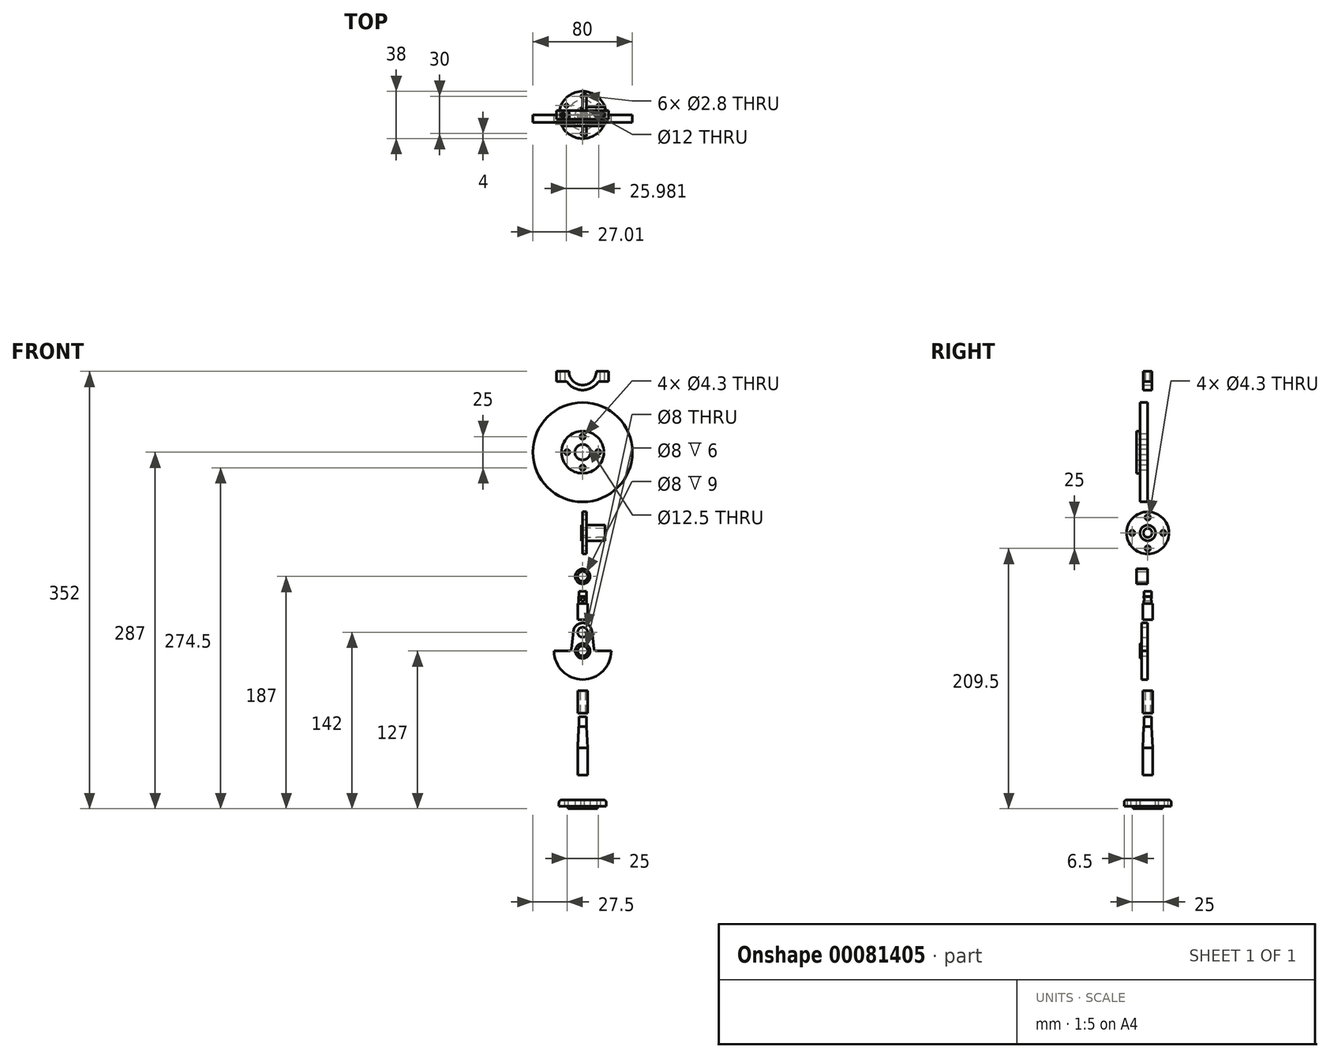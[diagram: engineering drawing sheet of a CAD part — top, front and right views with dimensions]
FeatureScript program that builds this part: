
annotation { "Feature Type Name" : "Feature", "Feature Type Description" : "" }
export const myFeature = defineFeature(function(context is Context, id is Id, definition is map)
    precondition{}
    {
        {
            var Q0;
            Q0=qCreatedBy(makeId("Top.planeOp"),FACE);
            var sketch = newSketch(context, id + "F0", { "sketchPlane" : qUnion([Q0])});
            skCircle(sketch, "E0", {"center": v(0, 0) * mm, "radius": 19 * mm});
            skCircle(sketch, "E1", {"center": v(0, 0) * mm, "radius": 6 * mm});
            skSolve(sketch);
        }
        {
            var Q0;
            Q0 = qSketchRegion(id + "F0", true);
            extrude(context, id + "F1", {"entities" : qUnion([Q0]), "depth" : 5 * mm});
        }
        {
            var Q0;
            Q0=makeQuery(id+"F1.opExtrude","CAP_FACE",FACE,{"disambiguationData":[OSD([sQuery(id+"F0.wireOp",EDGE,"E0"),sQuery(id+"F0.wireOp",EDGE,"E1")])],"isStart":true});
            var sketch = newSketch(context, id + "F2", { "sketchPlane" : qUnion([Q0])});
            skCircle(sketch, "E2", {"center": v(0, 0) * mm, "radius": 6 * mm});
            skCircle(sketch, "E3", {"center": v(0, 0) * mm, "radius": 12 * mm});
            skSolve(sketch);
        }
        {
            var Q0;
            Q0 = qSketchRegion(id + "F2", true);
            extrude(context, id + "F3", {"entities" : qUnion([Q0]), "operationType" : NewBodyOperationType.ADD, "depth" : 2 * mm});
        }
        {
            var Q0;
            Q0=makeQuery(id+"F1.opExtrude","CAP_EDGE",EDGE,{"disambiguationData":[OSD([sQuery(id+"F0.wireOp",EDGE,"E0")])],"isStart":false});
            fillet(context, id + "F4", {"entities" : qUnion([Q0]), "radius" : 2 * mm, "tangentPropagation" : true, "allowEdgeOverflow" : false});
        }
        {
            var Q0;
            Q0=makeQuery(id+"F1.opExtrude","CAP_FACE",FACE,{"disambiguationData":[OSD([sQuery(id+"F0.wireOp",EDGE,"E0"),sQuery(id+"F0.wireOp",EDGE,"E1")])],"isStart":false});
            var sketch = newSketch(context, id + "F5", { "sketchPlane" : qUnion([Q0])});
            skLineSegment(sketch, "E4", {"start": v(0, 0) * mm, "end": v(0, 15) * mm});
            skLineSegment(sketch, "E5.0", {"start": v(0, 15) * mm, "end": v(13, 7.5) * mm});
            skLineSegment(sketch, "E5.1", {"start": v(13, 7.5) * mm, "end": v(13, -7.5) * mm});
            skLineSegment(sketch, "E5.2", {"start": v(13, -7.5) * mm, "end": v(0, -15) * mm});
            skLineSegment(sketch, "E5.3", {"start": v(0, -15) * mm, "end": v(-13, -7.5) * mm});
            skLineSegment(sketch, "E5.4", {"start": v(-13, -7.5) * mm, "end": v(-13, 7.5) * mm});
            skLineSegment(sketch, "E5.5", {"start": v(-13, 7.5) * mm, "end": v(0, 15) * mm});
            skCircle(sketch, "E6", {"center": v(0, 15) * mm, "radius": 1.4 * mm});
            skCircle(sketch, "E7", {"center": v(-13, 7.5) * mm, "radius": 1.4 * mm});
            skCircle(sketch, "E8", {"center": v(-13, -7.5) * mm, "radius": 1.4 * mm});
            skCircle(sketch, "E9", {"center": v(0, -15) * mm, "radius": 1.4 * mm});
            skCircle(sketch, "E10", {"center": v(13, -7.5) * mm, "radius": 1.4 * mm});
            skCircle(sketch, "E11", {"center": v(13, 7.5) * mm, "radius": 1.4 * mm});
            skSolve(sketch);
        }
        {
            var Q0;
            {var subQ0=sQuery(id+"F5.wireOp",EDGE,"E5.5");var subQ1=sQuery(id+"F5.wireOp",EDGE,"E5.4");var subQ2=makeQuery(id+"F5.imprint","INTERSECT",VERTEX,{"derivedFrom":[subQ1,subQ0]});Q0=makeQuery(id+"F5.imprint","IMPRINT",FACE,{"disambiguationData":[TD([[makeQuery(id+"F5.imprint","IMPRINT",EDGE,{"disambiguationData":[TD([[subQ2,1.0]])],"derivedFrom":subQ1}),1.0]])]});}
            var Q1;
            {var subQ0=sQuery(id+"F5.wireOp",EDGE,"E5.5");var subQ1=sQuery(id+"F5.wireOp",EDGE,"E5.4");var subQ2=makeQuery(id+"F5.imprint","INTERSECT",VERTEX,{"derivedFrom":[subQ1,subQ0]});Q1=makeQuery(id+"F5.imprint","IMPRINT",FACE,{"disambiguationData":[TD([[makeQuery(id+"F5.imprint","IMPRINT",EDGE,{"disambiguationData":[TD([[subQ2,1.0]])],"derivedFrom":subQ1}),-1.0]])]});}
            var Q2;
            {var subQ1=sQuery(id+"F5.wireOp",EDGE,"E5.0");var subQ3=sQuery(id+"F5.wireOp",EDGE,"E6");var subQ4=makeQuery(id+"F5.imprint","INTERSECT",VERTEX,{"derivedFrom":[subQ1,subQ3]});Q2=makeQuery(id+"F5.imprint","IMPRINT",FACE,{"disambiguationData":[TD([[makeQuery(id+"F5.imprint","IMPRINT",EDGE,{"disambiguationData":[TD([[subQ4,-1.0]])],"derivedFrom":subQ3}),1.0]])]});}
            var Q3;
            {var subQ1=sQuery(id+"F5.wireOp",EDGE,"E4");var subQ3=sQuery(id+"F5.wireOp",EDGE,"E6");var subQ4=makeQuery(id+"F5.imprint","INTERSECT",VERTEX,{"derivedFrom":[subQ1,subQ3]});Q3=makeQuery(id+"F5.imprint","IMPRINT",FACE,{"disambiguationData":[TD([[makeQuery(id+"F5.imprint","IMPRINT",EDGE,{"disambiguationData":[TD([[subQ4,-1.0]])],"derivedFrom":subQ3}),1.0]])]});}
            var Q4;
            {var subQ1=sQuery(id+"F5.wireOp",EDGE,"E4");var subQ3=sQuery(id+"F5.wireOp",EDGE,"E6");var subQ4=makeQuery(id+"F5.imprint","INTERSECT",VERTEX,{"derivedFrom":[subQ1,subQ3]});Q4=makeQuery(id+"F5.imprint","IMPRINT",FACE,{"disambiguationData":[TD([[makeQuery(id+"F5.imprint","IMPRINT",EDGE,{"disambiguationData":[TD([[subQ4,1.0]])],"derivedFrom":subQ3}),1.0]])]});}
            var Q5;
            {var subQ0=sQuery(id+"F5.wireOp",EDGE,"E5.1");var subQ1=sQuery(id+"F5.wireOp",EDGE,"E5.0");var subQ2=makeQuery(id+"F5.imprint","INTERSECT",VERTEX,{"derivedFrom":[subQ1,subQ0]});Q5=makeQuery(id+"F5.imprint","IMPRINT",FACE,{"disambiguationData":[TD([[makeQuery(id+"F5.imprint","IMPRINT",EDGE,{"disambiguationData":[TD([[subQ2,1.0]])],"derivedFrom":subQ1}),1.0]])]});}
            var Q6;
            {var subQ0=sQuery(id+"F5.wireOp",EDGE,"E5.1");var subQ1=sQuery(id+"F5.wireOp",EDGE,"E5.0");var subQ2=makeQuery(id+"F5.imprint","INTERSECT",VERTEX,{"derivedFrom":[subQ1,subQ0]});Q6=makeQuery(id+"F5.imprint","IMPRINT",FACE,{"disambiguationData":[TD([[makeQuery(id+"F5.imprint","IMPRINT",EDGE,{"disambiguationData":[TD([[subQ2,1.0]])],"derivedFrom":subQ1}),-1.0]])]});}
            var Q7;
            {var subQ0=sQuery(id+"F5.wireOp",EDGE,"E5.2");var subQ1=sQuery(id+"F5.wireOp",EDGE,"E5.1");var subQ2=makeQuery(id+"F5.imprint","INTERSECT",VERTEX,{"derivedFrom":[subQ1,subQ0]});Q7=makeQuery(id+"F5.imprint","IMPRINT",FACE,{"disambiguationData":[TD([[makeQuery(id+"F5.imprint","IMPRINT",EDGE,{"disambiguationData":[TD([[subQ2,1.0]])],"derivedFrom":subQ1}),1.0]])]});}
            var Q8;
            {var subQ0=sQuery(id+"F5.wireOp",EDGE,"E5.2");var subQ1=sQuery(id+"F5.wireOp",EDGE,"E5.1");var subQ2=makeQuery(id+"F5.imprint","INTERSECT",VERTEX,{"derivedFrom":[subQ1,subQ0]});Q8=makeQuery(id+"F5.imprint","IMPRINT",FACE,{"disambiguationData":[TD([[makeQuery(id+"F5.imprint","IMPRINT",EDGE,{"disambiguationData":[TD([[subQ2,1.0]])],"derivedFrom":subQ1}),-1.0]])]});}
            var Q9;
            {var subQ0=sQuery(id+"F5.wireOp",EDGE,"E5.3");var subQ1=sQuery(id+"F5.wireOp",EDGE,"E5.2");var subQ2=makeQuery(id+"F5.imprint","INTERSECT",VERTEX,{"derivedFrom":[subQ1,subQ0]});Q9=makeQuery(id+"F5.imprint","IMPRINT",FACE,{"disambiguationData":[TD([[makeQuery(id+"F5.imprint","IMPRINT",EDGE,{"disambiguationData":[TD([[subQ2,1.0]])],"derivedFrom":subQ1}),1.0]])]});}
            var Q10;
            {var subQ0=sQuery(id+"F5.wireOp",EDGE,"E5.3");var subQ1=sQuery(id+"F5.wireOp",EDGE,"E5.2");var subQ2=makeQuery(id+"F5.imprint","INTERSECT",VERTEX,{"derivedFrom":[subQ1,subQ0]});Q10=makeQuery(id+"F5.imprint","IMPRINT",FACE,{"disambiguationData":[TD([[makeQuery(id+"F5.imprint","IMPRINT",EDGE,{"disambiguationData":[TD([[subQ2,1.0]])],"derivedFrom":subQ1}),-1.0]])]});}
            var Q11;
            {var subQ0=sQuery(id+"F5.wireOp",EDGE,"E5.4");var subQ1=sQuery(id+"F5.wireOp",EDGE,"E5.3");var subQ2=makeQuery(id+"F5.imprint","INTERSECT",VERTEX,{"derivedFrom":[subQ1,subQ0]});Q11=makeQuery(id+"F5.imprint","IMPRINT",FACE,{"disambiguationData":[TD([[makeQuery(id+"F5.imprint","IMPRINT",EDGE,{"disambiguationData":[TD([[subQ2,1.0]])],"derivedFrom":subQ1}),1.0]])]});}
            var Q12;
            {var subQ0=sQuery(id+"F5.wireOp",EDGE,"E5.4");var subQ1=sQuery(id+"F5.wireOp",EDGE,"E5.3");var subQ2=makeQuery(id+"F5.imprint","INTERSECT",VERTEX,{"derivedFrom":[subQ1,subQ0]});Q12=makeQuery(id+"F5.imprint","IMPRINT",FACE,{"disambiguationData":[TD([[makeQuery(id+"F5.imprint","IMPRINT",EDGE,{"disambiguationData":[TD([[subQ2,1.0]])],"derivedFrom":subQ1}),-1.0]])]});}
            extrude(context, id + "F6", {"entities" : qUnion([Q0, Q1, Q2, Q3, Q4, Q5, Q6, Q7, Q8, Q9, Q10, Q11, Q12]), "operationType" : NewBodyOperationType.REMOVE, "oppositeDirection" : true, "depth" : 25 * mm});
        }
        {
            var Q0;
            Q0=makeQuery(id+"F1.opExtrude","SWEPT_BODY",BODY,{"disambiguationData":[OSD([sQuery(id+"F0.wireOp",EDGE,"E0"),sQuery(id+"F0.wireOp",EDGE,"E1")])]});
            transform(context, id + "F7", {"entities" : qUnion([Q0]), "transformType" : TransformType.TRANSLATION_3D, "dx" : 0 * mm, "dy" : 0 * mm, "dz" : 100 * mm, "makeCopy" : false});
        }
        {
            var Q0;
            Q0=qCreatedBy(makeId("Front.planeOp"),FACE);
            var sketch = newSketch(context, id + "F8", { "sketchPlane" : qUnion([Q0])});
            skLineSegment(sketch, "E12", {"start": v(0, 0) * mm, "end": v(0, 22) * mm});
            skLineSegment(sketch, "E13", {"start": v(0, 22) * mm, "end": v(4, 22) * mm});
            skLineSegment(sketch, "E14", {"start": v(4, 22) * mm, "end": v(4, 0) * mm});
            skLineSegment(sketch, "E15", {"start": v(4, 0) * mm, "end": v(0, 0) * mm});
            skLineSegment(sketch, "E16", {"start": v(0, 0) * mm, "end": v(0, 39) * mm});
            skLineSegment(sketch, "E17", {"start": v(0, 39) * mm, "end": v(3.18, 39) * mm});
            skLineSegment(sketch, "E18", {"start": v(3.18, 39) * mm, "end": v(4, 22) * mm});
            skLineSegment(sketch, "E19", {"start": v(0, 0) * mm, "end": v(0, 47) * mm});
            skLineSegment(sketch, "E20", {"start": v(0, 47) * mm, "end": v(3, 47) * mm});
            skLineSegment(sketch, "E21", {"start": v(3, 47) * mm, "end": v(3, 39) * mm});
            skSolve(sketch);
        }
        {
            var Q0;
            Q0 = qSketchRegion(id + "F8", true);
            var Q1;
            Q1=sQuery(id+"F8.wireOp",EDGE,"E19");
            revolve(context, id + "F9", {"entities" : qUnion([Q0]), "axis" : qUnion([Q1]), "revolveType" : RevolveType.FULL});
        }
        {
            var Q0;
            Q0=makeQuery(id+"F9.opRevolve","SWEPT_BODY",BODY,{"disambiguationData":[OSD([sQuery(id+"F8.wireOp",EDGE,"E14"),sQuery(id+"F8.wireOp",EDGE,"E15"),sQuery(id+"F8.wireOp",EDGE,"E17"),sQuery(id+"F8.wireOp",EDGE,"E18"),sQuery(id+"F8.wireOp",EDGE,"E19"),sQuery(id+"F8.wireOp",EDGE,"E20"),sQuery(id+"F8.wireOp",EDGE,"E21")])]});
            transform(context, id + "F10", {"entities" : qUnion([Q0]), "transformType" : TransformType.TRANSLATION_3D, "dx" : 0 * mm, "dy" : 0 * mm, "dz" : 125 * mm, "makeCopy" : false});
        }
        {
            var Q0;
            Q0=qCreatedBy(makeId("Top.planeOp"),FACE);
            var sketch = newSketch(context, id + "F11", { "sketchPlane" : qUnion([Q0])});
            skCircle(sketch, "E22", {"center": v(0, 0) * mm, "radius": 2 * mm});
            skCircle(sketch, "E23", {"center": v(0, 0) * mm, "radius": 4 * mm});
            skSolve(sketch);
        }
        {
            var Q0;
            Q0 = qSketchRegion(id + "F11", true);
            extrude(context, id + "F12", {"entities" : qUnion([Q0]), "depth" : 18 * mm});
        }
        {
            var Q0;
            Q0=makeQuery(id+"F12.opExtrude","SWEPT_BODY",BODY,{"disambiguationData":[OSD([sQuery(id+"F11.wireOp",EDGE,"E22"),sQuery(id+"F11.wireOp",EDGE,"E23")])]});
            transform(context, id + "F13", {"entities" : qUnion([Q0]), "transformType" : TransformType.TRANSLATION_3D, "dx" : 0 * mm, "dy" : 0 * mm, "dz" : 175 * mm, "makeCopy" : false});
        }
        {
            var Q0;
            Q0=qCreatedBy(makeId("Front.planeOp"),FACE);
            var sketch = newSketch(context, id + "F14", { "sketchPlane" : qUnion([Q0])});
            skArc(sketch, "E24", {"start": v(-23, 0) * mm, "mid": v(0, -23) * mm, "end": v(23, 0) * mm});
            skLineSegment(sketch, "E25", {"start": v(-9.3, 0) * mm, "end": v(-23, 0) * mm});
            skLineSegment(sketch, "E26", {"start": v(-23, 0) * mm, "end": v(-9.3, 0) * mm});
            skCircle(sketch, "E27", {"center": v(0, 0) * mm, "radius": 4 * mm});
            skLineSegment(sketch, "E28.trimOffspring", {"start": v(11.08, 0) * mm, "end": v(23, 0) * mm});
            skCircle(sketch, "E29", {"center": v(0, 15) * mm, "radius": 4 * mm});
            skArc(sketch, "E30", {"start": v(7.45, 15.87) * mm, "mid": v(0, 22.5) * mm, "end": v(-7.45, 15.87) * mm});
            skLineSegment(sketch, "E31", {"start": v(-23, 0) * mm, "end": v(-11.3, 0) * mm});
            skLineSegment(sketch, "E32", {"start": v(-11.3, 0) * mm, "end": v(-11.3, 2.99) * mm});
            skLineSegment(sketch, "E33", {"start": v(-11.3, 0) * mm, "end": v(-11.08, 0) * mm});
            skLineSegment(sketch, "E34", {"start": v(-9.1, 1.77) * mm, "end": v(-7.45, 15.87) * mm});
            skPoint(sketch, "E35.visualSharp", {"position": v(-9.3, 0) * mm});
            skArc(sketch, "E35.filletArc", {"start": v(-11.08, 0) * mm, "mid": v(-9.75, 0.5) * mm, "end": v(-9.1, 1.77) * mm});
            skArc(sketch, "E36.MirrorCS", {"start": v(11.08, 0) * mm, "mid": v(9.75, 0.5) * mm, "end": v(9.1, 1.77) * mm});
            skLineSegment(sketch, "E37.MirrorCS", {"start": v(9.1, 1.77) * mm, "end": v(7.45, 15.87) * mm});
            skSolve(sketch);
        }
        {
            var Q0;
            Q0=makeQuery(id+"F14.imprint","IMPRINT",FACE,{"disambiguationData":[TD([[makeQuery(id+"F14.imprint","IMPRINT",EDGE,{"derivedFrom":sQuery(id+"F14.wireOp",EDGE,"E24")}),1.0]])]});
            extrude(context, id + "F15", {"entities" : qUnion([Q0]), "depth" : 5 * mm});
        }
        {
            var Q0;
            Q0=makeQuery(id+"F15.opExtrude","CAP_FACE",FACE,{"disambiguationData":[OSD([sQuery(id+"F14.wireOp",EDGE,"E24"),sQuery(id+"F14.wireOp",EDGE,"E27"),sQuery(id+"F14.wireOp",EDGE,"E28.trimOffspring"),sQuery(id+"F14.wireOp",EDGE,"E29"),sQuery(id+"F14.wireOp",EDGE,"E30"),sQuery(id+"F14.wireOp",EDGE,"E31"),sQuery(id+"F14.wireOp",EDGE,"E33"),sQuery(id+"F14.wireOp",EDGE,"E34"),sQuery(id+"F14.wireOp",EDGE,"E35.filletArc"),sQuery(id+"F14.wireOp",EDGE,"E36.MirrorCS"),sQuery(id+"F14.wireOp",EDGE,"E37.MirrorCS")])],"isStart":false});
            var sketch = newSketch(context, id + "F16", { "sketchPlane" : qUnion([Q0])});
            skCircle(sketch, "E38", {"center": v(0, 0) * mm, "radius": 6 * mm});
            skCircle(sketch, "E39", {"center": v(0, 0) * mm, "radius": 4 * mm});
            skSolve(sketch);
        }
        {
            var Q0;
            Q0 = qSketchRegion(id + "F16", true);
            extrude(context, id + "F17", {"entities" : qUnion([Q0]), "operationType" : NewBodyOperationType.ADD, "depth" : 1 * mm});
        }
        {
            var Q0;
            Q0=makeQuery(id+"F15.opExtrude","SWEPT_BODY",BODY,{"disambiguationData":[OSD([sQuery(id+"F14.wireOp",EDGE,"E24"),sQuery(id+"F14.wireOp",EDGE,"E27"),sQuery(id+"F14.wireOp",EDGE,"E28.trimOffspring"),sQuery(id+"F14.wireOp",EDGE,"E29"),sQuery(id+"F14.wireOp",EDGE,"E30"),sQuery(id+"F14.wireOp",EDGE,"E31"),sQuery(id+"F14.wireOp",EDGE,"E33"),sQuery(id+"F14.wireOp",EDGE,"E34"),sQuery(id+"F14.wireOp",EDGE,"E35.filletArc"),sQuery(id+"F14.wireOp",EDGE,"E36.MirrorCS"),sQuery(id+"F14.wireOp",EDGE,"E37.MirrorCS")])]});
            transform(context, id + "F18", {"entities" : qUnion([Q0]), "transformType" : TransformType.TRANSLATION_3D, "dx" : 0 * mm, "dy" : 0 * mm, "dz" : 225 * mm, "makeCopy" : false});
        }
        {
            var Q0;
            Q0=qCreatedBy(makeId("Front.planeOp"),FACE);
            var sketch = newSketch(context, id + "F19", { "sketchPlane" : qUnion([Q0])});
            skLineSegment(sketch, "E40", {"start": v(0, 0) * mm, "end": v(4, 0) * mm});
            skLineSegment(sketch, "E41", {"start": v(4, 0) * mm, "end": v(4, 13) * mm});
            skLineSegment(sketch, "E42", {"start": v(4, 13) * mm, "end": v(3.17, 13) * mm});
            skLineSegment(sketch, "E43", {"start": v(0, 13) * mm, "end": v(0, 0) * mm});
            skLineSegment(sketch, "E44", {"start": v(0, 0) * mm, "end": v(0, 19) * mm});
            skLineSegment(sketch, "E45", {"start": v(3, 19) * mm, "end": v(3.17, 19) * mm});
            skLineSegment(sketch, "E46", {"start": v(3.17, 19) * mm, "end": v(3.17, 13) * mm});
            skLineSegment(sketch, "E47", {"start": v(0, 0) * mm, "end": v(0, 23) * mm});
            skLineSegment(sketch, "E48", {"start": v(0, 23) * mm, "end": v(3, 23) * mm});
            skLineSegment(sketch, "E49", {"start": v(3, 23) * mm, "end": v(3, 19) * mm});
            skSolve(sketch);
        }
        {
            var Q0;
            Q0 = qSketchRegion(id + "F19", true);
            var Q1;
            Q1=sQuery(id+"F19.wireOp",EDGE,"E47");
            revolve(context, id + "F20", {"entities" : qUnion([Q0]), "axis" : qUnion([Q1]), "revolveType" : RevolveType.FULL});
        }
        {
            var Q0;
            Q0=qCreatedBy(makeId("Front.planeOp"),FACE);
            var sketch = newSketch(context, id + "F21", { "sketchPlane" : qUnion([Q0])});
            skLineSegment(sketch, "E50", {"start": v(0, 0) * mm, "end": v(0, 16.55) * mm});
            skCircle(sketch, "E51", {"center": v(0, 16.55) * mm, "radius": 1.5 * mm});
            skSolve(sketch);
        }
        {
            var Q0;
            Q0 = qSketchRegion(id + "F21", true);
            extrude(context, id + "F22", {"entities" : qUnion([Q0]), "operationType" : NewBodyOperationType.REMOVE, "endBound" : BoundingType.SYMMETRIC, "oppositeDirection" : true, "depth" : 25 * mm});
        }
        {
            var Q0;
            Q0=makeQuery(id+"F20.opRevolve","SWEPT_BODY",BODY,{"disambiguationData":[OSD([sQuery(id+"F19.wireOp",EDGE,"E40"),sQuery(id+"F19.wireOp",EDGE,"E41"),sQuery(id+"F19.wireOp",EDGE,"E42"),sQuery(id+"F19.wireOp",EDGE,"E45"),sQuery(id+"F19.wireOp",EDGE,"E46"),sQuery(id+"F19.wireOp",EDGE,"E47"),sQuery(id+"F19.wireOp",EDGE,"E48"),sQuery(id+"F19.wireOp",EDGE,"E49")])]});
            transform(context, id + "F23", {"entities" : qUnion([Q0]), "transformType" : TransformType.TRANSLATION_3D, "dx" : 0 * mm, "dy" : 0 * mm, "dz" : 250 * mm, "makeCopy" : false});
        }
        {
            var Q0;
            Q0=qCreatedBy(makeId("Front.planeOp"),FACE);
            var sketch = newSketch(context, id + "F24", { "sketchPlane" : qUnion([Q0])});
            skCircle(sketch, "E52", {"center": v(0, 0) * mm, "radius": 4 * mm});
            skCircle(sketch, "E53", {"center": v(0, 0) * mm, "radius": 6 * mm});
            skSolve(sketch);
        }
        {
            var Q0;
            Q0 = qSketchRegion(id + "F24", true);
            extrude(context, id + "F25", {"entities" : qUnion([Q0]), "depth" : 9 * mm});
        }
        {
            var Q0;
            Q0=makeQuery(id+"F25.opExtrude","SWEPT_BODY",BODY,{"disambiguationData":[OSD([sQuery(id+"F24.wireOp",EDGE,"E52"),sQuery(id+"F24.wireOp",EDGE,"E53")])]});
            transform(context, id + "F26", {"entities" : qUnion([Q0]), "transformType" : TransformType.TRANSLATION_3D, "dx" : 0 * mm, "dy" : 0 * mm, "dz" : 285 * mm, "makeCopy" : false});
        }
        {
            var Q0;
            Q0=qCreatedBy(makeId("Front.planeOp"),FACE);
            var sketch = newSketch(context, id + "F27", { "sketchPlane" : qUnion([Q0])});
            skLineSegment(sketch, "E54", {"start": v(0, 0) * mm, "end": v(-1, 0) * mm});
            skLineSegment(sketch, "E55", {"start": v(-1, 0) * mm, "end": v(-1, 6.25) * mm});
            skLineSegment(sketch, "E56", {"start": v(-1, 6.25) * mm, "end": v(0, 6.25) * mm});
            skLineSegment(sketch, "E57", {"start": v(0, 6.25) * mm, "end": v(0, 3.97) * mm});
            skLineSegment(sketch, "E58", {"start": v(0, 3.97) * mm, "end": v(0, 17) * mm});
            skLineSegment(sketch, "E59", {"start": v(0, 17) * mm, "end": v(3, 17) * mm});
            skLineSegment(sketch, "E60", {"start": v(3, 17) * mm, "end": v(3, 3.89) * mm});
            skLineSegment(sketch, "E61", {"start": v(3, 0) * mm, "end": v(0, 0) * mm});
            skLineSegment(sketch, "E62", {"start": v(3, 3.89) * mm, "end": v(3, 6.25) * mm});
            skLineSegment(sketch, "E63", {"start": v(3, 6.25) * mm, "end": v(18, 6.25) * mm});
            skLineSegment(sketch, "E64", {"start": v(18, 6.25) * mm, "end": v(18, 3.47) * mm});
            skLineSegment(sketch, "E65", {"start": v(18, 0) * mm, "end": v(3, 0) * mm});
            skLineSegment(sketch, "E66", {"start": v(-1, 0) * mm, "end": v(-1, 4) * mm});
            skLineSegment(sketch, "E67", {"start": v(18, 3.47) * mm, "end": v(-1, 4) * mm});
            skSolve(sketch);
        }
        {
            var Q0;
            Q0 = qSketchRegion(id + "F27", true);
            var Q1;
            Q1=sQuery(id+"F27.wireOp",EDGE,"E61");
            revolve(context, id + "F28", {"entities" : qUnion([Q0]), "axis" : qUnion([Q1]), "revolveType" : RevolveType.FULL});
        }
        {
            var Q0;
            Q0=makeQuery(id+"F28.opRevolve","SWEPT_FACE",FACE,{"disambiguationData":[OSD([sQuery(id+"F27.wireOp",EDGE,"E58")])]});
            var sketch = newSketch(context, id + "F29", { "sketchPlane" : qUnion([Q0])});
            skCircle(sketch, "E68", {"center": v(0, 12.5) * mm, "radius": 2.15 * mm});
            skLineSegment(sketch, "E69", {"start": v(0, 0) * mm, "end": v(1.8, 0) * mm});
            skLineSegment(sketch, "E70", {"start": v(0, 0) * mm, "end": v(0, 2.48) * mm});
            skCircle(sketch, "E71.MirrorC", {"center": v(0, -12.5) * mm, "radius": 2.15 * mm});
            skLineSegment(sketch, "E72", {"start": v(0, 0) * mm, "end": v(12.5, 0) * mm});
            skCircle(sketch, "E73", {"center": v(12.5, 0) * mm, "radius": 2.15 * mm});
            skCircle(sketch, "E74.MirrorC", {"center": v(-12.5, 0) * mm, "radius": 2.15 * mm});
            skSolve(sketch);
        }
        {
            var Q0;
            Q0 = qSketchRegion(id + "F29", true);
            extrude(context, id + "F30", {"entities" : qUnion([Q0]), "operationType" : NewBodyOperationType.REMOVE, "oppositeDirection" : true, "depth" : 25 * mm});
        }
        {
            var Q0;
            Q0=makeQuery(id+"F28.opRevolve","SWEPT_BODY",BODY,{"disambiguationData":[OSD([sQuery(id+"F27.wireOp",EDGE,"E55"),sQuery(id+"F27.wireOp",EDGE,"E56"),sQuery(id+"F27.wireOp",EDGE,"E58"),sQuery(id+"F27.wireOp",EDGE,"E59"),sQuery(id+"F27.wireOp",EDGE,"E60"),sQuery(id+"F27.wireOp",EDGE,"E63"),sQuery(id+"F27.wireOp",EDGE,"E64"),sQuery(id+"F27.wireOp",EDGE,"E67")])]});
            transform(context, id + "F31", {"entities" : qUnion([Q0]), "transformType" : TransformType.TRANSLATION_3D, "dx" : 0 * mm, "dy" : 0 * mm, "dz" : 320 * mm, "makeCopy" : false});
        }
        {
            var Q0;
            Q0=qCreatedBy(makeId("Front.planeOp"),FACE);
            var sketch = newSketch(context, id + "F32", { "sketchPlane" : qUnion([Q0])});
            skCircle(sketch, "E75", {"center": v(0, 0) * mm, "radius": 40 * mm});
            skCircle(sketch, "E76", {"center": v(0, 0) * mm, "radius": 6.25 * mm});
            skSolve(sketch);
        }
        {
            var Q0;
            Q0 = qSketchRegion(id + "F32", true);
            extrude(context, id + "F33", {"entities" : qUnion([Q0]), "depth" : 6 * mm});
        }
        {
            var Q0;
            Q0=makeQuery(id+"F33.opExtrude","CAP_FACE",FACE,{"disambiguationData":[OSD([sQuery(id+"F32.wireOp",EDGE,"E75"),sQuery(id+"F32.wireOp",EDGE,"E76")])],"isStart":false});
            var sketch = newSketch(context, id + "F34", { "sketchPlane" : qUnion([Q0])});
            skCircle(sketch, "E77", {"center": v(0, 0) * mm, "radius": 17 * mm});
            skCircle(sketch, "E78", {"center": v(0, 0) * mm, "radius": 6.25 * mm});
            skSolve(sketch);
        }
        {
            var Q0;
            Q0 = qSketchRegion(id + "F34", true);
            extrude(context, id + "F35", {"entities" : qUnion([Q0]), "operationType" : NewBodyOperationType.ADD, "depth" : 3 * mm});
        }
        {
            var Q0;
            Q0=makeQuery(id+"F35.opExtrude","CAP_FACE",FACE,{"disambiguationData":[OSD([sQuery(id+"F34.wireOp",EDGE,"E77"),sQuery(id+"F34.wireOp",EDGE,"E78")])],"isStart":false});
            var sketch = newSketch(context, id + "F36", { "sketchPlane" : qUnion([Q0])});
            skCircle(sketch, "E79", {"center": v(0, 12.5) * mm, "radius": 2.15 * mm});
            skCircle(sketch, "E80", {"center": v(12.5, 0) * mm, "radius": 2.15 * mm});
            skCircle(sketch, "E81.MirrorC", {"center": v(0, -12.5) * mm, "radius": 2.15 * mm});
            skCircle(sketch, "E82.MirrorC", {"center": v(-12.5, 0) * mm, "radius": 2.15 * mm});
            skSolve(sketch);
        }
        {
            var Q0;
            Q0 = qSketchRegion(id + "F36", true);
            extrude(context, id + "F37", {"entities" : qUnion([Q0]), "operationType" : NewBodyOperationType.REMOVE, "oppositeDirection" : true, "depth" : 25 * mm});
        }
        {
            var Q0;
            Q0=makeQuery(id+"F33.opExtrude","SWEPT_BODY",BODY,{"disambiguationData":[OSD([sQuery(id+"F32.wireOp",EDGE,"E75"),sQuery(id+"F32.wireOp",EDGE,"E76")])]});
            transform(context, id + "F38", {"entities" : qUnion([Q0]), "transformType" : TransformType.TRANSLATION_3D, "dx" : 0 * mm, "dy" : 0 * mm, "dz" : 385 * mm, "makeCopy" : false});
        }
        {
            var Q0;
            Q0=qCreatedBy(makeId("Front.planeOp"),FACE);
            var sketch = newSketch(context, id + "F39", { "sketchPlane" : qUnion([Q0])});
            skArc(sketch, "E83", {"start": v(-11, 0) * mm, "mid": v(0, -11) * mm, "end": v(11, 0) * mm});
            skArc(sketch, "E84", {"start": v(-15, 0) * mm, "mid": v(0, -15) * mm, "end": v(15, 0) * mm});
            skLineSegment(sketch, "E85", {"start": v(-15, 0) * mm, "end": v(-11, 0) * mm});
            skLineSegment(sketch, "E86.trimOffspring", {"start": v(11, 0) * mm, "end": v(15, 0) * mm});
            skLineSegment(sketch, "E87", {"start": v(-11, 0) * mm, "end": v(-21, 0) * mm});
            skLineSegment(sketch, "E88", {"start": v(-21, 0) * mm, "end": v(-21, -8) * mm});
            skLineSegment(sketch, "E89", {"start": v(-21, -8) * mm, "end": v(-12.7, -8) * mm});
            skLineSegment(sketch, "E90", {"start": v(-12.7, -8) * mm, "end": v(-11.77, -7.54) * mm});
            skLineSegment(sketch, "E91", {"start": v(0, 0) * mm, "end": v(0, 2.3) * mm});
            skLineSegment(sketch, "E92.MirrorCS", {"start": v(21, -8) * mm, "end": v(12.7, -8) * mm});
            skLineSegment(sketch, "E93.MirrorCS", {"start": v(21, 0) * mm, "end": v(21, -8) * mm});
            skLineSegment(sketch, "E94.MirrorCS", {"start": v(11, 0) * mm, "end": v(21, 0) * mm});
            skLineSegment(sketch, "E95.MirrorCS", {"start": v(12.7, -8) * mm, "end": v(11.77, -7.54) * mm});
            skSolve(sketch);
        }
        {
            var Q0;
            {var subQ5=sQuery(id+"F39.wireOp",EDGE,"E83");Q0=makeQuery(id+"F39.imprint","IMPRINT",FACE,{"disambiguationData":[TD([[makeQuery(id+"F39.imprint","IMPRINT",EDGE,{"derivedFrom":subQ5}),-1.0]])]});}
            var Q1;
            {var subQ1=sQuery(id+"F39.wireOp",EDGE,"E88");Q1=makeQuery(id+"F39.imprint","IMPRINT",FACE,{"disambiguationData":[TD([[makeQuery(id+"F39.imprint","IMPRINT",EDGE,{"derivedFrom":subQ1}),1.0]])]});}
            var Q2;
            {var subQ4=sQuery(id+"F39.wireOp",EDGE,"E92.MirrorCS");Q2=makeQuery(id+"F39.imprint","IMPRINT",FACE,{"disambiguationData":[TD([[makeQuery(id+"F39.imprint","IMPRINT",EDGE,{"derivedFrom":subQ4}),-1.0]])]});}
            extrude(context, id + "F40", {"entities" : qUnion([Q0, Q1, Q2]), "endBound" : BoundingType.SYMMETRIC, "depth" : 7 * mm});
        }
        {
            var Q0;
            Q0=makeQuery(id+"F40.opExtrude","SWEPT_FACE",FACE,{"disambiguationData":[OSD([sQuery(id+"F39.wireOp",EDGE,"E87")])]});
            var sketch = newSketch(context, id + "F41", { "sketchPlane" : qUnion([Q0])});
            skLineSegment(sketch, "E96", {"start": v(0, 0) * mm, "end": v(-16, 0) * mm});
            skCircle(sketch, "E97", {"center": v(-16, 0) * mm, "radius": 1.8 * mm});
            skLineSegment(sketch, "E98", {"start": v(0, 0) * mm, "end": v(0, -4.91) * mm});
            skCircle(sketch, "E99.MirrorC", {"center": v(16, 0) * mm, "radius": 1.8 * mm});
            skSolve(sketch);
        }
        {
            var Q0;
            Q0 = qSketchRegion(id + "F41", true);
            extrude(context, id + "F42", {"entities" : qUnion([Q0]), "operationType" : NewBodyOperationType.REMOVE, "oppositeDirection" : true, "depth" : 25 * mm});
        }
        {
            var Q0;
            Q0=makeQuery(id+"F40.opExtrude","SWEPT_BODY",BODY,{"disambiguationData":[OSD([sQuery(id+"F39.wireOp",EDGE,"E83"),sQuery(id+"F39.wireOp",EDGE,"E84"),sQuery(id+"F39.wireOp",EDGE,"E87"),sQuery(id+"F39.wireOp",EDGE,"E88"),sQuery(id+"F39.wireOp",EDGE,"E89"),sQuery(id+"F39.wireOp",EDGE,"E90"),sQuery(id+"F39.wireOp",EDGE,"E92.MirrorCS"),sQuery(id+"F39.wireOp",EDGE,"E93.MirrorCS"),sQuery(id+"F39.wireOp",EDGE,"E94.MirrorCS"),sQuery(id+"F39.wireOp",EDGE,"E95.MirrorCS")])]});
            transform(context, id + "F43", {"entities" : qUnion([Q0]), "transformType" : TransformType.TRANSLATION_3D, "dx" : 0 * mm, "dy" : 0 * mm, "dz" : 450 * mm, "makeCopy" : false});
        }
    });
